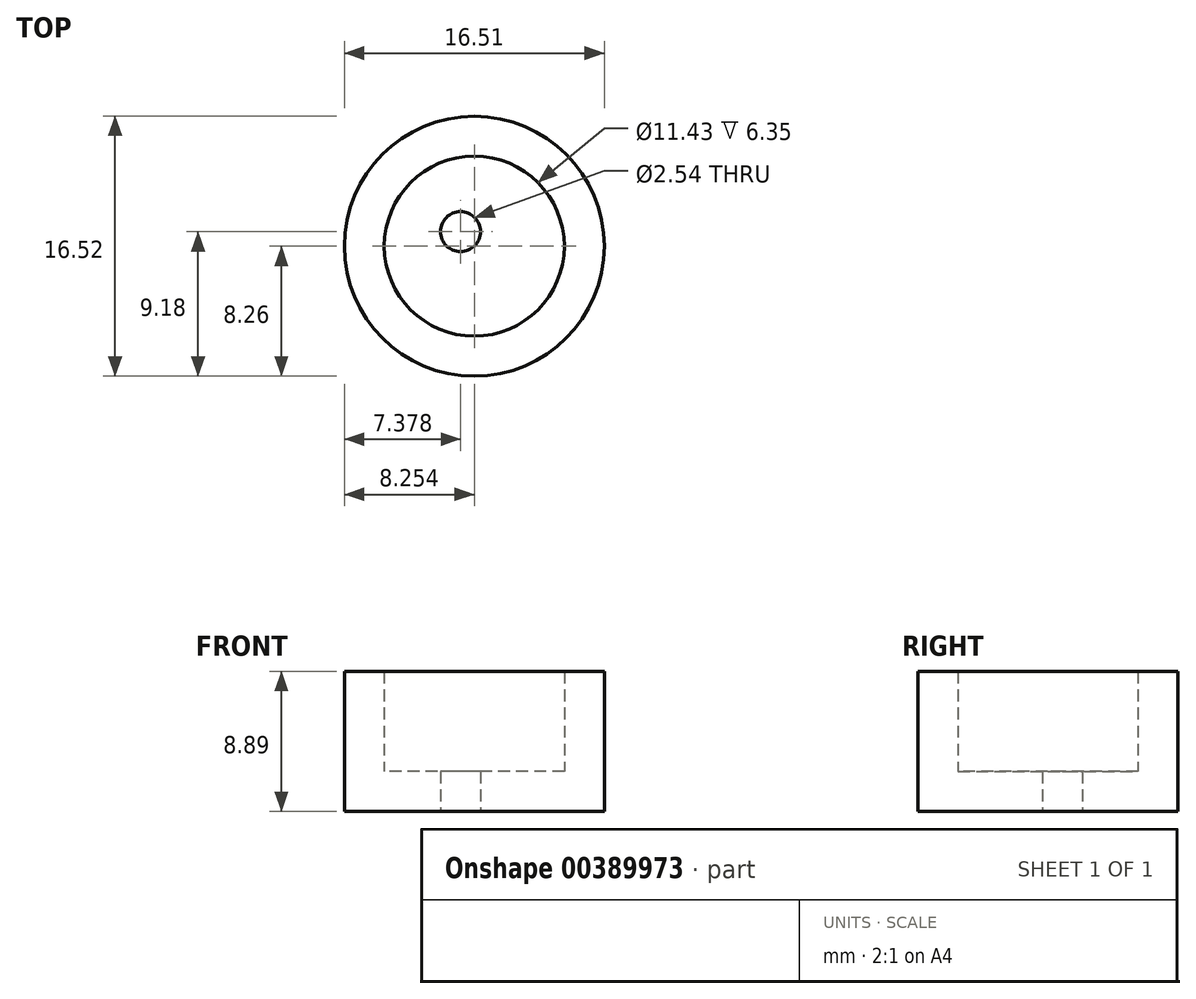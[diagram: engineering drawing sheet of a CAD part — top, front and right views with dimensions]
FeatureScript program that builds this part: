
annotation { "Feature Type Name" : "Feature", "Feature Type Description" : "" }
export const myFeature = defineFeature(function(context is Context, id is Id, definition is map)
    precondition{}
    {
        {
            var Q0;
            Q0=qCreatedBy(makeId("Top.planeOp"),FACE);
            var sketch = newSketch(context, id + "F0", { "sketchPlane" : qUnion([Q0])});
            skLineSegment(sketch, "E0", {"start": v(0, 0) * mm, "end": v(-23.59, 0) * mm});
            skCircle(sketch, "E1", {"center": v(-23.59, 0) * mm, "radius": 8.26 * mm});
            skSolve(sketch);
        }
        {
            var Q0;
            Q0=makeQuery(id+"F0.imprint","IMPRINT",FACE,{"disambiguationData":[TD([[makeQuery(id+"F0.imprint","IMPRINT",EDGE,{"derivedFrom":sQuery(id+"F0.wireOp",EDGE,"E1")}),1.0]])]});
            extrude(context, id + "F1", {"entities" : qUnion([Q0]), "depth" : 8.9 * mm});
        }
        {
            var Q0;
            Q0=makeQuery(id+"F1.opExtrude","CAP_FACE",FACE,{"disambiguationData":[OSD([sQuery(id+"F0.wireOp",EDGE,"E1")])],"isStart":false});
            shell(context, id + "F2", {"entities" : qUnion([Q0]), "thickness" : 2.54 * mm});
        }
        {
            var Q0;
            Q0=makeQuery(id+"F1.opExtrude","CAP_FACE",FACE,{"disambiguationData":[OSD([sQuery(id+"F0.wireOp",EDGE,"E1")])],"isStart":true});
            var sketch = newSketch(context, id + "F3", { "sketchPlane" : qUnion([Q0])});
            skLineSegment(sketch, "E2", {"start": v(-24.46, -0.92) * mm, "end": v(-24.46, -8.2) * mm});
            skCircle(sketch, "E3", {"center": v(-24.46, -0.92) * mm, "radius": 1.27 * mm});
            skSolve(sketch);
        }
        {
            var Q0;
            Q0=makeQuery(id+"F3.imprint","IMPRINT",FACE,{"disambiguationData":[TD([[makeQuery(id+"F3.imprint","IMPRINT",EDGE,{"derivedFrom":sQuery(id+"F3.wireOp",EDGE,"E3")}),1.0]])]});
            extrude(context, id + "F4", {"entities" : qUnion([Q0]), "operationType" : NewBodyOperationType.REMOVE, "oppositeDirection" : true, "depth" : 25.4 * mm});
        }
    });
